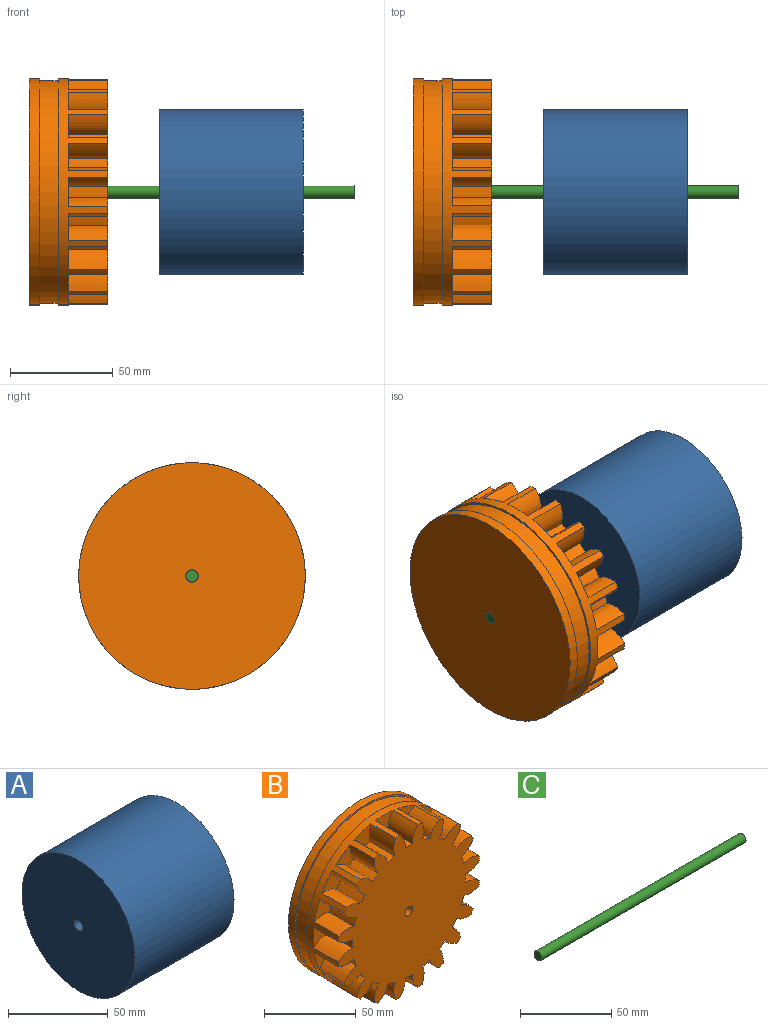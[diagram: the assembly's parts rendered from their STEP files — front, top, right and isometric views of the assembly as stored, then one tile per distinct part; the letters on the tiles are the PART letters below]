
ASSEMBLY  parts=3 mates=2
PART A: 4 faces, bbox 70x80x80 mm
  f0: cylinder r=3mm len=70mm, axis (-1,0,0), area 1319.5mm2, adj f2,f3
  f1: cylinder r=40mm len=80mm, axis (-1,0,0), area 17592.9mm2, adj f2,f3
  f2: plane 80x80mm, normal (1,0,0), area 4998.3mm2, adj f0,f1
  f3: plane 80x80mm, normal (-1,0,0), area 4998.3mm2, adj f0,f1
PART B: 90 faces, bbox 110x38x110 mm
  f0: extruded ~13.77x5mm, area 69mm2, adj f2,f86,f88
  f1: cylinder r=55mm len=110mm, axis (0,-1,0), area 1658.8mm2, adj f84,f85,f89
  f2: cylinder r=55mm len=110mm, axis (0,-1,0), area 2978.1mm2, adj f0,f3,f5,f7,f8,f10,f11,f13
  f3: plane 109.36x109.36mm, normal (0,-1,0), area 7635.4mm2, adj f2,f4,f5,f6,f7,f8,f9,f10
  f4: cylinder r=3mm len=38mm, axis (0,-1,0), area 716.3mm2, adj f3,f85
  f5: extruded ~19x10.91mm, area 227.6mm2, adj f2,f3,f6,f74
  f6: cylinder r=43.75mm len=19mm, axis (0,-1,0), area 105.8mm2, adj f3,f5,f7,f74
  f7: extruded ~19x10.91mm, area 227.6mm2, adj f2,f3,f6,f74
  f8: extruded ~19x11.24mm, area 227.6mm2, adj f2,f3,f9,f76
  f9: cylinder r=43.75mm len=19mm, axis (0,-1,0), area 105.8mm2, adj f3,f8,f10,f76
  f10: extruded ~19x9.73mm, area 227.6mm2, adj f2,f3,f9,f76
  f11: extruded ~19x9.73mm, area 227.6mm2, adj f2,f3,f12,f77
  f12: cylinder r=43.75mm len=19mm, axis (0,-1,0), area 105.8mm2, adj f3,f11,f13,f77
  f13: extruded ~19x11.24mm, area 227.6mm2, adj f2,f3,f12,f77
  f14: extruded ~19x11.64mm, area 227.6mm2, adj f2,f3,f15,f75
  f15: cylinder r=43.75mm len=19mm, axis (0,-1,0), area 105.8mm2, adj f3,f14,f16,f75
  f16: extruded ~19x9.1mm, area 227.6mm2, adj f2,f3,f15,f75
  f17: extruded ~19x11.24mm, area 227.6mm2, adj f2,f3,f18,f71
  f18: cylinder r=43.75mm len=19mm, axis (0,-1,0), area 105.8mm2, adj f3,f17,f19,f71
  f19: extruded ~19x9.73mm, area 227.6mm2, adj f2,f3,f18,f71
  f20: extruded ~19x11.64mm, area 227.6mm2, adj f2,f3,f21,f70
  f21: cylinder r=43.75mm len=19mm, axis (0,-1,0), area 105.8mm2, adj f3,f20,f22,f70
  f22: extruded ~19x9.1mm, area 227.6mm2, adj f2,f3,f21,f70
  f23: extruded ~19x9.1mm, area 227.6mm2, adj f2,f3,f24,f73
  f24: cylinder r=43.75mm len=19mm, axis (0,-1,0), area 105.8mm2, adj f3,f23,f25,f73
  f25: extruded ~19x11.64mm, area 227.6mm2, adj f2,f3,f24,f73
  f26: extruded ~19x9.73mm, area 227.6mm2, adj f2,f3,f27,f72
  f27: cylinder r=43.75mm len=19mm, axis (0,-1,0), area 105.8mm2, adj f3,f26,f28,f72
  f28: extruded ~19x11.24mm, area 227.6mm2, adj f2,f3,f27,f72
  f29: extruded ~19x9.73mm, area 227.6mm2, adj f2,f3,f30,f67
  f30: cylinder r=43.75mm len=19mm, axis (0,-1,0), area 105.8mm2, adj f3,f29,f31,f67
  f31: extruded ~19x11.24mm, area 227.6mm2, adj f2,f3,f30,f67
  f32: extruded ~19x11.24mm, area 227.6mm2, adj f2,f3,f33,f66
  f33: cylinder r=43.75mm len=19mm, axis (0,-1,0), area 105.8mm2, adj f3,f32,f34,f66
  f34: extruded ~19x9.73mm, area 227.6mm2, adj f2,f3,f33,f66
  f35: extruded ~19x9.1mm, area 227.6mm2, adj f2,f3,f36,f68
  f36: cylinder r=43.75mm len=19mm, axis (0,-1,0), area 105.8mm2, adj f3,f35,f37,f68
  f37: extruded ~19x11.64mm, area 227.6mm2, adj f2,f3,f36,f68
  f38: extruded ~19x10.91mm, area 227.6mm2, adj f2,f3,f39,f69
  f39: cylinder r=43.75mm len=19mm, axis (0,-1,0), area 105.8mm2, adj f3,f38,f40,f69
  f40: extruded ~19x10.91mm, area 227.6mm2, adj f2,f3,f39,f69
  f41: extruded ~19x9.1mm, area 227.6mm2, adj f2,f3,f42,f78
  f42: cylinder r=43.75mm len=19mm, axis (0,-1,0), area 105.8mm2, adj f3,f41,f43,f78
  f43: extruded ~19x11.64mm, area 227.6mm2, adj f2,f3,f42,f78
  f44: extruded ~19x10.91mm, area 227.6mm2, adj f2,f3,f45,f79
  f45: cylinder r=43.75mm len=19mm, axis (0,-1,0), area 105.8mm2, adj f3,f44,f46,f79
  f46: extruded ~19x10.91mm, area 227.6mm2, adj f2,f3,f45,f79
  f47: extruded ~19x11.24mm, area 227.6mm2, adj f2,f3,f48,f81
  f48: cylinder r=43.75mm len=19mm, axis (0,-1,0), area 105.8mm2, adj f3,f47,f49,f81
  f49: extruded ~19x9.73mm, area 227.6mm2, adj f2,f3,f48,f81
  f50: extruded ~19x11.64mm, area 227.6mm2, adj f2,f3,f51,f80
  f51: cylinder r=43.75mm len=19mm, axis (0,-1,0), area 105.8mm2, adj f3,f50,f52,f80
  f52: extruded ~19x9.1mm, area 227.6mm2, adj f2,f3,f51,f80
  f53: extruded ~19x9.1mm, area 227.6mm2, adj f2,f3,f54,f83
  f54: cylinder r=43.75mm len=19mm, axis (0,-1,0), area 105.8mm2, adj f3,f53,f55,f83
  f55: extruded ~19x11.64mm, area 227.6mm2, adj f2,f3,f54,f83
  f56: extruded ~19x9.73mm, area 227.6mm2, adj f2,f3,f57,f82
  f57: cylinder r=43.75mm len=19mm, axis (0,-1,0), area 105.8mm2, adj f3,f56,f58,f82
  f58: extruded ~19x11.24mm, area 227.6mm2, adj f2,f3,f57,f82
  f59: extruded ~19x10.91mm, area 227.6mm2, adj f2,f3,f60,f86
  f60: cylinder r=43.75mm len=19mm, axis (0,-1,0), area 105.8mm2, adj f3,f59,f61,f86
  f61: extruded ~19x10.91mm, area 227.6mm2, adj f2,f3,f60,f86
  f62: extruded ~19x11.64mm, area 227.6mm2, adj f2,f3,f63,f65
  f63: cylinder r=43.75mm len=19mm, axis (0,-1,0), area 105.8mm2, adj f3,f62,f64,f65
  f64: extruded ~19x9.1mm, area 227.6mm2, adj f2,f3,f63,f65
  f65: plane 13.47x13.32mm, normal (0,-1,0), area 92mm2, adj f2,f62,f63,f64
  f66: plane 14.62x14.34mm, normal (0,-1,0), area 92mm2, adj f2,f32,f33,f34
  f67: plane 14.62x14.34mm, normal (0,-1,0), area 92mm2, adj f2,f29,f30,f31
  f68: plane 13.47x13.32mm, normal (0,-1,0), area 92mm2, adj f2,f35,f36,f37
  f69: plane 13.99x11.34mm, normal (0,-1,0), area 92mm2, adj f2,f38,f39,f40
  f70: plane 13.47x13.32mm, normal (0,-1,0), area 92mm2, adj f2,f20,f21,f22
  f71: plane 14.62x14.34mm, normal (0,-1,0), area 92mm2, adj f2,f17,f18,f19
  f72: plane 14.62x14.34mm, normal (0,-1,0), area 92mm2, adj f2,f26,f27,f28
  f73: plane 13.47x13.32mm, normal (0,-1,0), area 92mm2, adj f2,f23,f24,f25
  f74: plane 13.99x11.34mm, normal (0,-1,0), area 92mm2, adj f2,f5,f6,f7
  f75: plane 13.47x13.32mm, normal (0,-1,0), area 92mm2, adj f2,f14,f15,f16
  f76: plane 14.62x14.34mm, normal (0,-1,0), area 92mm2, adj f2,f8,f9,f10
  f77: plane 14.62x14.34mm, normal (0,-1,0), area 92mm2, adj f2,f11,f12,f13
  f78: plane 13.47x13.32mm, normal (0,-1,0), area 92mm2, adj f2,f41,f42,f43
  f79: plane 13.99x11.34mm, normal (0,-1,0), area 92mm2, adj f2,f44,f45,f46
  f80: plane 13.47x13.32mm, normal (0,-1,0), area 92mm2, adj f2,f50,f51,f52
  f81: plane 14.62x14.34mm, normal (0,-1,0), area 92mm2, adj f2,f47,f48,f49
  f82: plane 14.62x14.34mm, normal (0,-1,0), area 92mm2, adj f2,f56,f57,f58
  f83: plane 13.47x13.32mm, normal (0,-1,0), area 92mm2, adj f2,f53,f54,f55
  f84: extruded ~13.77x5mm, area 69mm2, adj f1,f85,f89
  f85: plane 110x110mm, normal (0,1,0), area 9475mm2, adj f1,f4,f84
  f86: plane 13.99x11.34mm, normal (0,-1,0), area 92mm2, adj f0,f59,f60,f61
  f87: cylinder r=54mm len=108mm, axis (0,1,0), area 3053.6mm2, adj f88,f89
  f88: plane 110x110mm, normal (0,1,0), area 342.4mm2, adj f0,f2,f87
  f89: plane 110x110mm, normal (0,-1,0), area 342.4mm2, adj f1,f84,f87
PART C: 3 faces, bbox 158x6x6 mm
  f0: cylinder r=3mm len=158mm, axis (1,0,0), area 2978.2mm2, adj f1,f2
  f1: plane 6x6mm, normal (-1,0,0), area 28.3mm2, adj f0
  f2: plane 6x6mm, normal (1,0,0), area 28.3mm2, adj f0
PLACE A t=(18.22,32.43,50.67)mm
PLACE B rot(axis=(0.58,-0.58,0.58),120deg) t=(-41.78,32.43,110.67)mm
PLACE C t=(18.22,32.43,50.67)mm
MATE fastened C.f0 <-> A.f0  axis (1,0,0) through (78.22,32.43,110.67)mm
MATE fastened B.f1 <-> C.f0  axis (-1,0,0) through (-79.78,32.43,110.67)mm
